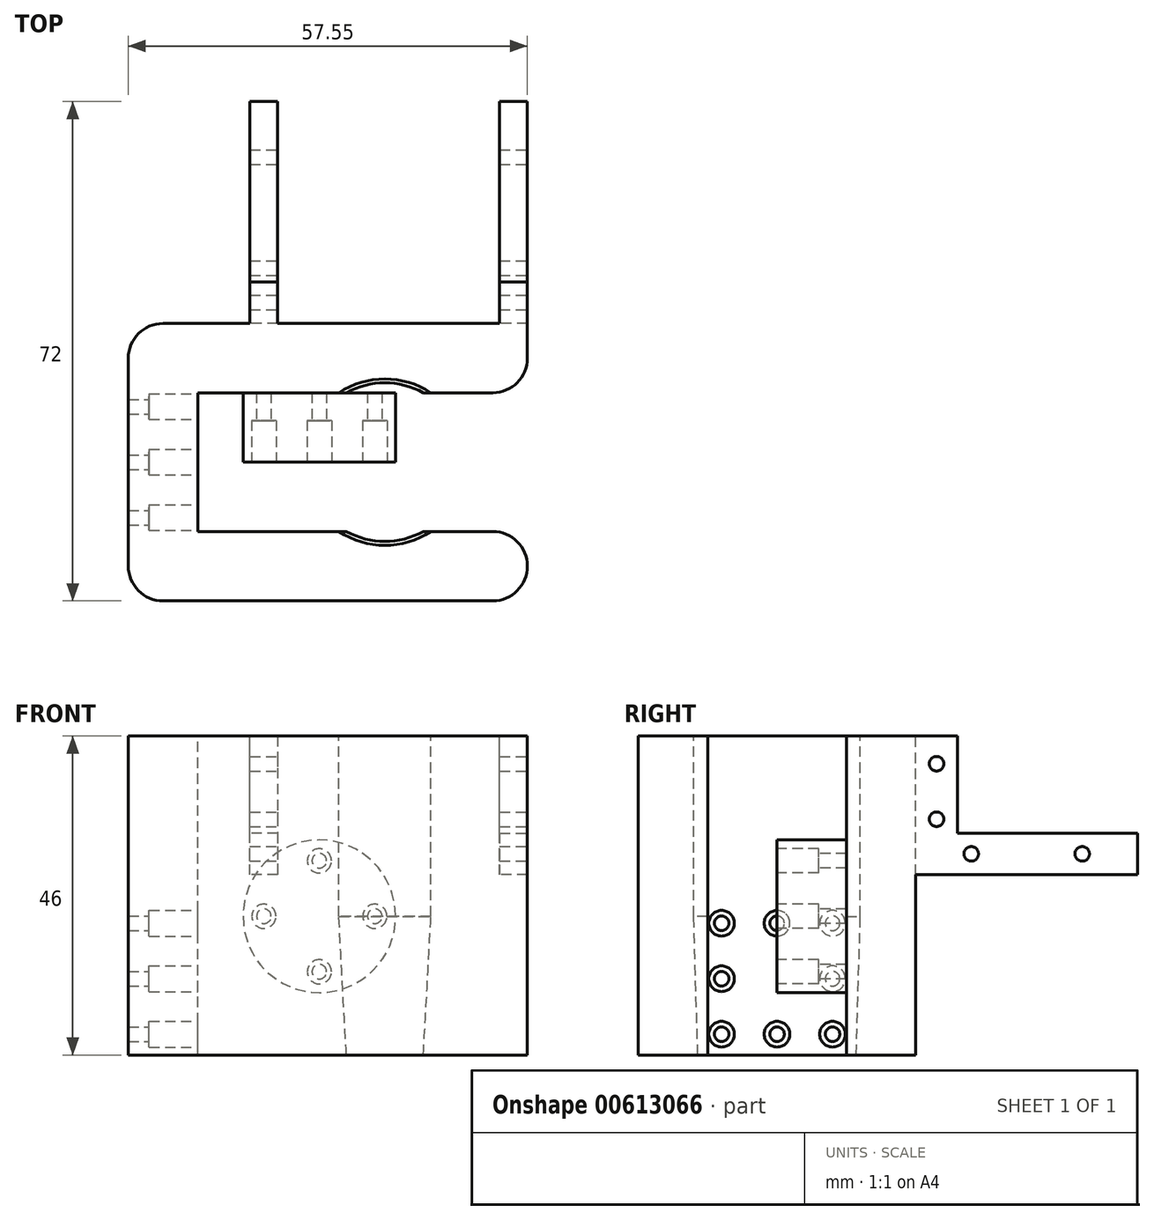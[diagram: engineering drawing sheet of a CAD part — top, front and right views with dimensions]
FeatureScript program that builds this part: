
annotation { "Feature Type Name" : "Feature", "Feature Type Description" : "" }
export const myFeature = defineFeature(function(context is Context, id is Id, definition is map)
    precondition{}
    {
        {
            var Q0;
            Q0=qCreatedBy(makeId("Top.planeOp"),FACE);
            var sketch = newSketch(context, id + "F0", { "sketchPlane" : qUnion([Q0])});
            skLineSegment(sketch, "E0", {"start": v(-27.55, 20) * mm, "end": v(30, 20) * mm});
            skLineSegment(sketch, "E1", {"start": v(30, 20) * mm, "end": v(30, -20) * mm});
            skLineSegment(sketch, "E2", {"start": v(30, -20) * mm, "end": v(-27.55, -20) * mm});
            skPoint(sketch, "E3.visualSharp", {"position": v(-27.55, 20) * mm});
            skPoint(sketch, "E4.visualSharp", {"position": v(30, 20) * mm});
            skPoint(sketch, "E5.visualSharp", {"position": v(30, -20) * mm});
            skPoint(sketch, "E6.visualSharp", {"position": v(-27.55, -20) * mm});
            skLineSegment(sketch, "E7", {"start": v(30, 10) * mm, "end": v(-17.55, 10) * mm});
            skLineSegment(sketch, "E8", {"start": v(-17.55, 10) * mm, "end": v(-17.55, -10) * mm});
            skLineSegment(sketch, "E9", {"start": v(-17.55, -10) * mm, "end": v(30, -10) * mm});
            skPoint(sketch, "E10", {"position": v(9.45, 0) * mm});
            skLineSegment(sketch, "E11", {"start": v(-27.55, -20) * mm, "end": v(-27.55, 20) * mm});
            skSolve(sketch);
        }
        {
            var Q0;
            Q0=makeQuery(id+"F0.imprint","IMPRINT",FACE,{"disambiguationData":[TD([[makeQuery(id+"F0.imprint","IMPRINT",EDGE,{"derivedFrom":sQuery(id+"F0.wireOp",EDGE,"E0")}),-1.0]])]});
            extrude(context, id + "F1", {"entities" : qUnion([Q0]), "oppositeDirection" : true, "depth" : 20 * mm, "offsetDistance" : 25 * mm});
        }
        {
            var Q0;
            Q0=makeQuery(id+"F0.imprint","IMPRINT",FACE,{"disambiguationData":[TD([[makeQuery(id+"F0.imprint","IMPRINT",EDGE,{"derivedFrom":sQuery(id+"F0.wireOp",EDGE,"E0")}),-1.0]])]});
            extrude(context, id + "F2", {"entities" : qUnion([Q0]), "operationType" : NewBodyOperationType.ADD, "depth" : 26 * mm, "offsetDistance" : 25 * mm});
        }
        {
            var Q0;
            Q0=sQuery(id+"F0.wireOp",VERTEX,"E10");
            var Q1;
            Q1=makeQuery(id+"F1.opExtrude","SWEPT_FACE",FACE,{"disambiguationData":[OSD([sQuery(id+"F0.wireOp",EDGE,"E8")])]});
            cPlane(context, id + "F3", {"entities" : qUnion([Q0, Q1]), "cplaneType" : CPlaneType.PLANE_POINT, "offset" : 25 * mm, "width" : 150 * mm, "height" : 150 * mm});
        }
        {
            var Q0;
            Q0=qCreatedBy(id+"F3.planeOp",FACE);
            var sketch = newSketch(context, id + "F4", { "sketchPlane" : qUnion([Q0])});
            skLineSegment(sketch, "E12", {"start": v(0, 0) * mm, "end": v(0, -20) * mm});
            skLineSegment(sketch, "E13", {"start": v(0, -20) * mm, "end": v(11.43, -20) * mm});
            skLineSegment(sketch, "E14", {"start": v(11.43, -20) * mm, "end": v(12, 0) * mm});
            skLineSegment(sketch, "E15", {"start": v(12, 0) * mm, "end": v(0, 0) * mm});
            skLineSegment(sketch, "E16", {"start": v(0, 0) * mm, "end": v(0, 26) * mm});
            skLineSegment(sketch, "E17", {"start": v(0, 26) * mm, "end": v(12, 26) * mm});
            skLineSegment(sketch, "E18", {"start": v(12, 26) * mm, "end": v(12, 0) * mm});
            skSolve(sketch);
        }
        {
            var Q0;
            Q0=makeQuery(id+"F4.imprint","IMPRINT",FACE,{"disambiguationData":[TD([[makeQuery(id+"F4.imprint","IMPRINT",EDGE,{"derivedFrom":sQuery(id+"F4.wireOp",EDGE,"E12")}),1.0]])]});
            var Q1;
            Q1=sQuery(id+"F4.wireOp",EDGE,"E12");
            revolve(context, id + "F5", {"operationType" : NewBodyOperationType.REMOVE, "entities" : qUnion([Q0]), "axis" : qUnion([Q1]), "revolveType" : RevolveType.FULL, "oppositeDirection" : true});
        }
        {
            var Q0;
            Q0=makeQuery(id+"F4.imprint","IMPRINT",FACE,{"disambiguationData":[TD([[makeQuery(id+"F4.imprint","IMPRINT",EDGE,{"derivedFrom":sQuery(id+"F4.wireOp",EDGE,"E15")}),-1.0]])]});
            var Q1;
            Q1=sQuery(id+"F4.wireOp",EDGE,"E16");
            revolve(context, id + "F6", {"operationType" : NewBodyOperationType.REMOVE, "entities" : qUnion([Q0]), "axis" : qUnion([Q1]), "revolveType" : RevolveType.FULL, "oppositeDirection" : true});
        }
        {
            var Q0;
            {var subQ0=sQuery(id+"F0.wireOp",EDGE,"E0");Q0=makeQuery(id+"F2.boolean.opBoolean","MERGE",FACE,{"derivedFrom":[makeQuery(id+"F1.opExtrude","SWEPT_FACE",FACE,{"disambiguationData":[OSD([subQ0])]}),makeQuery(id+"F2.opExtrude","SWEPT_FACE",FACE,{"disambiguationData":[OSD([subQ0])]})]});}
            var sketch = newSketch(context, id + "F7", { "sketchPlane" : qUnion([Q0])});
            skLineSegment(sketch, "E19", {"start": v(-30, 6) * mm, "end": v(-26, 6) * mm});
            skLineSegment(sketch, "E20", {"start": v(-26, 6) * mm, "end": v(-26, 26) * mm});
            skLineSegment(sketch, "E21", {"start": v(6, 26) * mm, "end": v(6, 6) * mm});
            skLineSegment(sketch, "E22", {"start": v(6, 6) * mm, "end": v(10, 6) * mm});
            skLineSegment(sketch, "E23", {"start": v(10, 6) * mm, "end": v(10, 26) * mm});
            skSolve(sketch);
        }
        {
            var Q0;
            {var subQ0=sQuery(id+"F0.wireOp",EDGE,"E9");var subQ1=sQuery(id+"F0.wireOp",EDGE,"E1");Q0=makeQuery(id+"F2.boolean.opBoolean","MERGE",EDGE,{"derivedFrom":[makeQuery(id+"F1.opExtrude","SWEPT_EDGE",EDGE,{"disambiguationData":[OSD([subQ1,subQ0])]}),makeQuery(id+"F2.opExtrude","SWEPT_EDGE",EDGE,{"disambiguationData":[OSD([subQ1,subQ0])]})]});}
            var Q1;
            {var subQ0=sQuery(id+"F0.wireOp",EDGE,"E7");var subQ1=sQuery(id+"F0.wireOp",EDGE,"E1");Q1=makeQuery(id+"F2.boolean.opBoolean","MERGE",EDGE,{"derivedFrom":[makeQuery(id+"F1.opExtrude","SWEPT_EDGE",EDGE,{"disambiguationData":[OSD([subQ1,subQ0])]}),makeQuery(id+"F2.opExtrude","SWEPT_EDGE",EDGE,{"disambiguationData":[OSD([subQ1,subQ0])]})]});}
            var Q2;
            {var subQ0=sQuery(id+"F0.wireOp",EDGE,"E2");var subQ1=sQuery(id+"F0.wireOp",EDGE,"E1");Q2=makeQuery(id+"F2.boolean.opBoolean","MERGE",EDGE,{"derivedFrom":[makeQuery(id+"F1.opExtrude","SWEPT_EDGE",EDGE,{"disambiguationData":[OSD([subQ1,subQ0])]}),makeQuery(id+"F2.opExtrude","SWEPT_EDGE",EDGE,{"disambiguationData":[OSD([subQ1,subQ0])]})]});}
            var Q3;
            {var subQ0=sQuery(id+"F0.wireOp",EDGE,"E11");var subQ1=sQuery(id+"F0.wireOp",EDGE,"E2");Q3=makeQuery(id+"F2.boolean.opBoolean","MERGE",EDGE,{"derivedFrom":[makeQuery(id+"F1.opExtrude","SWEPT_EDGE",EDGE,{"disambiguationData":[OSD([subQ1,subQ0])]}),makeQuery(id+"F2.opExtrude","SWEPT_EDGE",EDGE,{"disambiguationData":[OSD([subQ1,subQ0])]})]});}
            var Q4;
            {var subQ0=sQuery(id+"F0.wireOp",EDGE,"woha816s-cTYS-9xIi-TLmN-vEKe9L8YFnLm");var subQ1=sQuery(id+"F0.wireOp",EDGE,"yoHehqiI-3B4o-eTnI-9dCb-dK3FpP0ffTJ5");Q4=makeQuery(id+"F2.boolean.opBoolean","MERGE",EDGE,{"derivedFrom":[makeQuery(id+"F1.opExtrude","SWEPT_EDGE",EDGE,{"disambiguationData":[OSD([subQ1,subQ0])]}),makeQuery(id+"F2.opExtrude","SWEPT_EDGE",EDGE,{"disambiguationData":[OSD([subQ1,subQ0])]})]});}
            var Q5;
            {var subQ0=sQuery(id+"F0.wireOp",EDGE,"E11");var subQ1=sQuery(id+"F0.wireOp",EDGE,"E0");Q5=makeQuery(id+"F2.boolean.opBoolean","MERGE",EDGE,{"derivedFrom":[makeQuery(id+"F1.opExtrude","SWEPT_EDGE",EDGE,{"disambiguationData":[OSD([subQ1,subQ0])]}),makeQuery(id+"F2.opExtrude","SWEPT_EDGE",EDGE,{"disambiguationData":[OSD([subQ1,subQ0])]})]});}
            fillet(context, id + "F8", {"entities" : qUnion([Q0, Q1, Q2, Q3, Q4, Q5]), "radius" : 5 * mm, "tangentPropagation" : true, "allowEdgeOverflow" : false});
        }
        {
            var Q0;
            {var subQ0=sQuery(id+"F7.wireOp",EDGE,"E19");Q0=makeQuery(id+"F7.imprint","IMPRINT",FACE,{"disambiguationData":[TD([[makeQuery(id+"F7.imprint","IMPRINT",EDGE,{"derivedFrom":subQ0}),1.0]])]});}
            var Q1;
            {var subQ0=sQuery(id+"F7.wireOp",EDGE,"E21");Q1=makeQuery(id+"F7.imprint","IMPRINT",FACE,{"disambiguationData":[TD([[makeQuery(id+"F7.imprint","IMPRINT",EDGE,{"derivedFrom":subQ0}),1.0]])]});}
            extrude(context, id + "F9", {"entities" : qUnion([Q0, Q1]), "operationType" : NewBodyOperationType.ADD, "depth" : 6 * mm, "offsetDistance" : 25 * mm});
        }
        {
            var Q0;
            Q0=makeQuery(id+"F9.opExtrude","CAP_FACE",FACE,{"disambiguationData":[OSD([sQuery(id+"F0.wireOp",EDGE,"E0"),sQuery(id+"F7.wireOp",EDGE,"E21"),sQuery(id+"F7.wireOp",EDGE,"E22"),sQuery(id+"F7.wireOp",EDGE,"E23")])],"isStart":false});
            var sketch = newSketch(context, id + "F10", { "sketchPlane" : qUnion([Q0])});
            skLineSegment(sketch, "E24", {"start": v(-26, 12) * mm, "end": v(-30, 12) * mm});
            skLineSegment(sketch, "E25", {"start": v(6, 12) * mm, "end": v(10, 12) * mm});
            skLineSegment(sketch, "E26", {"start": v(-26, 12) * mm, "end": v(-26, 6) * mm});
            skLineSegment(sketch, "E27", {"start": v(-26, 6) * mm, "end": v(-30, 6) * mm});
            skLineSegment(sketch, "E28", {"start": v(-30, 6) * mm, "end": v(-30, 12) * mm});
            skSolve(sketch);
        }
        {
            var Q0;
            Q0=makeQuery(id+"F10.imprint","IMPRINT",FACE,{"disambiguationData":[TD([[makeQuery(id+"F10.imprint","IMPRINT",EDGE,{"derivedFrom":sQuery(id+"F10.wireOp",EDGE,"E24")}),1.0]])]});
            var Q1;
            {var subQ0=sQuery(id+"F10.wireOp",EDGE,"E25");Q1=makeQuery(id+"F10.imprint","IMPRINT",FACE,{"disambiguationData":[TD([[makeQuery(id+"F10.imprint","IMPRINT",EDGE,{"derivedFrom":subQ0}),-1.0]])]});}
            extrude(context, id + "F11", {"entities" : qUnion([Q0, Q1]), "operationType" : NewBodyOperationType.ADD, "depth" : 26 * mm, "offsetDistance" : 25 * mm});
        }
        {
            var Q0;
            {var subQ0=sQuery(id+"F0.wireOp",EDGE,"E1");var subQ1=sQuery(id+"F0.wireOp",EDGE,"E0");var subQ2=makeQuery(id+"F0.imprint","IMPRINT",EDGE,{"disambiguationData":[TD([[makeQuery(id+"F0.imprint","INTERSECT",VERTEX,{"derivedFrom":[subQ1,subQ0]}),-1.0]])],"derivedFrom":subQ0});Q0=makeQuery(id+"F11.boolean.opBoolean","MERGE",FACE,{"derivedFrom":[makeQuery(id+"F9.boolean.opBoolean","MERGE",FACE,{"derivedFrom":[makeQuery(id+"F2.boolean.opBoolean","MERGE",FACE,{"derivedFrom":[makeQuery(id+"F1.opExtrude","SWEPT_FACE",FACE,{"disambiguationData":[OSD([subQ0]),TDD([subQ2])]}),makeQuery(id+"F2.opExtrude","SWEPT_FACE",FACE,{"disambiguationData":[OSD([subQ0]),TDD([subQ2])]})]}),makeQuery(id+"F9.opExtrude","SWEPT_FACE",FACE,{"disambiguationData":[OSD([subQ1,subQ0])]})]}),makeQuery(id+"F11.opExtrude","SWEPT_FACE",FACE,{"disambiguationData":[OSD([sQuery(id+"F10.wireOp",EDGE,"E28")])]})]});}
            var sketch = newSketch(context, id + "F12", { "sketchPlane" : qUnion([Q0])});
            skPoint(sketch, "E29", {"position": v(23, 22) * mm});
            skPoint(sketch, "E30", {"position": v(23, 14) * mm});
            skPoint(sketch, "E31", {"position": v(44, 9) * mm});
            skPoint(sketch, "E31.positionSnap0", {"position": v(52, 9) * mm});
            skPoint(sketch, "E32", {"position": v(28, 9) * mm});
            skSolve(sketch);
        }
        {
            var Q0;
            Q0=sQuery(id+"F12.wireOp",VERTEX,"E29");
            var Q1;
            Q1=sQuery(id+"F12.wireOp",VERTEX,"E30");
            var Q2;
            Q2=sQuery(id+"F12.wireOp",VERTEX,"E32");
            var Q3;
            Q3=sQuery(id+"F12.wireOp",VERTEX,"E31");
            var Q4;
            Q4=makeQuery(id+"F1.opExtrude","SWEPT_BODY",BODY,{"disambiguationData":[OSD([sQuery(id+"F0.wireOp",EDGE,"E0"),sQuery(id+"F0.wireOp",EDGE,"E1"),sQuery(id+"F0.wireOp",EDGE,"E2"),sQuery(id+"F0.wireOp",EDGE,"E7"),sQuery(id+"F0.wireOp",EDGE,"E8"),sQuery(id+"F0.wireOp",EDGE,"E9"),sQuery(id+"F0.wireOp",EDGE,"yoHehqiI-3B4o-eTnI-9dCb-dK3FpP0ffTJ5"),sQuery(id+"F0.wireOp",EDGE,"E11"),sQuery(id+"F0.wireOp",EDGE,"woha816s-cTYS-9xIi-TLmN-vEKe9L8YFnLm")])]});
            hole(context, id + "F13", {"style" : HoleStyle.SIMPLE, "endStyle" : HoleEndStyle.THROUGH, "holeDiameter" : 2.1 * mm, "majorDiameter" : 5 * mm, "isTappedThrough" : true, "tappedDepth" : 12 * mm, "tapClearance" : 3, "locations" : qUnion([Q0, Q1, Q2, Q3]), "scope" : qUnion([Q4])});
        }
        {
            var Q0;
            Q0=qCreatedBy(makeId("Front.planeOp"),FACE);
            var sketch = newSketch(context, id + "F14", { "sketchPlane" : qUnion([Q0])});
            skCircle(sketch, "E33", {"center": v(0, 0) * mm, "radius": 11 * mm});
            skCircle(sketch, "E34", {"center": v(0, 0) * mm, "radius": 8 * mm, "construction": true});
            skPoint(sketch, "E35", {"position": v(0, 8) * mm});
            skPoint(sketch, "E36", {"position": v(8, 0) * mm});
            skPoint(sketch, "E37", {"position": v(0, -8) * mm});
            skPoint(sketch, "E38", {"position": v(-8, 0) * mm});
            skSolve(sketch);
        }
        {
            var Q0;
            Q0 = qSketchRegion(id + "F14", true);
            extrude(context, id + "F15", {"entities" : qUnion([Q0]), "oppositeDirection" : true, "depth" : 10 * mm, "offsetDistance" : 25 * mm});
        }
        {
            var Q0;
            Q0=sQuery(id+"F14.wireOp",VERTEX,"E35");
            var Q1;
            Q1=sQuery(id+"F14.wireOp",VERTEX,"E36");
            var Q2;
            Q2=sQuery(id+"F14.wireOp",VERTEX,"E37");
            var Q3;
            Q3=sQuery(id+"F14.wireOp",VERTEX,"E38");
            var Q4;
            Q4=makeQuery(id+"F15.opExtrude","SWEPT_BODY",BODY,{"disambiguationData":[OSD([sQuery(id+"F14.wireOp",EDGE,"E33")])]});
            hole(context, id + "F16", {"style" : HoleStyle.C_BORE, "endStyle" : HoleEndStyle.THROUGH, "holeDiameter" : 2.1 * mm, "cBoreDiameter" : 3.5 * mm, "cBoreDepth" : 6 * mm, "majorDiameter" : 5 * mm, "isTappedThrough" : true, "tappedDepth" : 12 * mm, "tapClearance" : 3, "locations" : qUnion([Q0, Q1, Q2, Q3]), "scope" : qUnion([Q4])});
        }
        {
            var Q0;
            {var subQ0=sQuery(id+"F0.wireOp",EDGE,"E8");Q0=makeQuery(id+"F2.boolean.opBoolean","MERGE",FACE,{"derivedFrom":[makeQuery(id+"F1.opExtrude","SWEPT_FACE",FACE,{"disambiguationData":[OSD([subQ0])]}),makeQuery(id+"F2.opExtrude","SWEPT_FACE",FACE,{"disambiguationData":[OSD([subQ0])]})]});}
            var sketch = newSketch(context, id + "F17", { "sketchPlane" : qUnion([Q0])});
            skPoint(sketch, "E39", {"position": v(0, -17) * mm});
            skPoint(sketch, "E40", {"position": v(8, -17) * mm});
            skPoint(sketch, "E41", {"position": v(-8, -17) * mm});
            skPoint(sketch, "E42", {"position": v(-8, -9) * mm});
            skPoint(sketch, "E43", {"position": v(-8, -1) * mm});
            skPoint(sketch, "E44", {"position": v(0, -1) * mm});
            skPoint(sketch, "E45", {"position": v(8, -1) * mm});
            skPoint(sketch, "E46", {"position": v(8, -9) * mm});
            skSolve(sketch);
        }
        {
            var Q0;
            Q0=sQuery(id+"F17.wireOp",VERTEX,"E43");
            var Q1;
            Q1=sQuery(id+"F17.wireOp",VERTEX,"E44");
            var Q2;
            Q2=sQuery(id+"F17.wireOp",VERTEX,"E45");
            var Q3;
            Q3=sQuery(id+"F17.wireOp",VERTEX,"E46");
            var Q4;
            Q4=sQuery(id+"F17.wireOp",VERTEX,"E40");
            var Q5;
            Q5=sQuery(id+"F17.wireOp",VERTEX,"E39");
            var Q6;
            Q6=sQuery(id+"F17.wireOp",VERTEX,"E41");
            var Q7;
            Q7=sQuery(id+"F17.wireOp",VERTEX,"E42");
            var Q8;
            Q8=makeQuery(id+"F1.opExtrude","SWEPT_BODY",BODY,{"disambiguationData":[OSD([sQuery(id+"F0.wireOp",EDGE,"E0"),sQuery(id+"F0.wireOp",EDGE,"E1"),sQuery(id+"F0.wireOp",EDGE,"E2"),sQuery(id+"F0.wireOp",EDGE,"E7"),sQuery(id+"F0.wireOp",EDGE,"E8"),sQuery(id+"F0.wireOp",EDGE,"E9"),sQuery(id+"F0.wireOp",EDGE,"E11")])]});
            hole(context, id + "F18", {"style" : HoleStyle.C_BORE, "endStyle" : HoleEndStyle.THROUGH, "holeDiameter" : 2.1 * mm, "cBoreDiameter" : 3.7 * mm, "cBoreDepth" : 7 * mm, "majorDiameter" : 5 * mm, "isTappedThrough" : true, "tappedDepth" : 12 * mm, "tapClearance" : 3, "locations" : qUnion([Q0, Q1, Q2, Q3, Q4, Q5, Q6, Q7]), "scope" : qUnion([Q8])});
        }
    });
